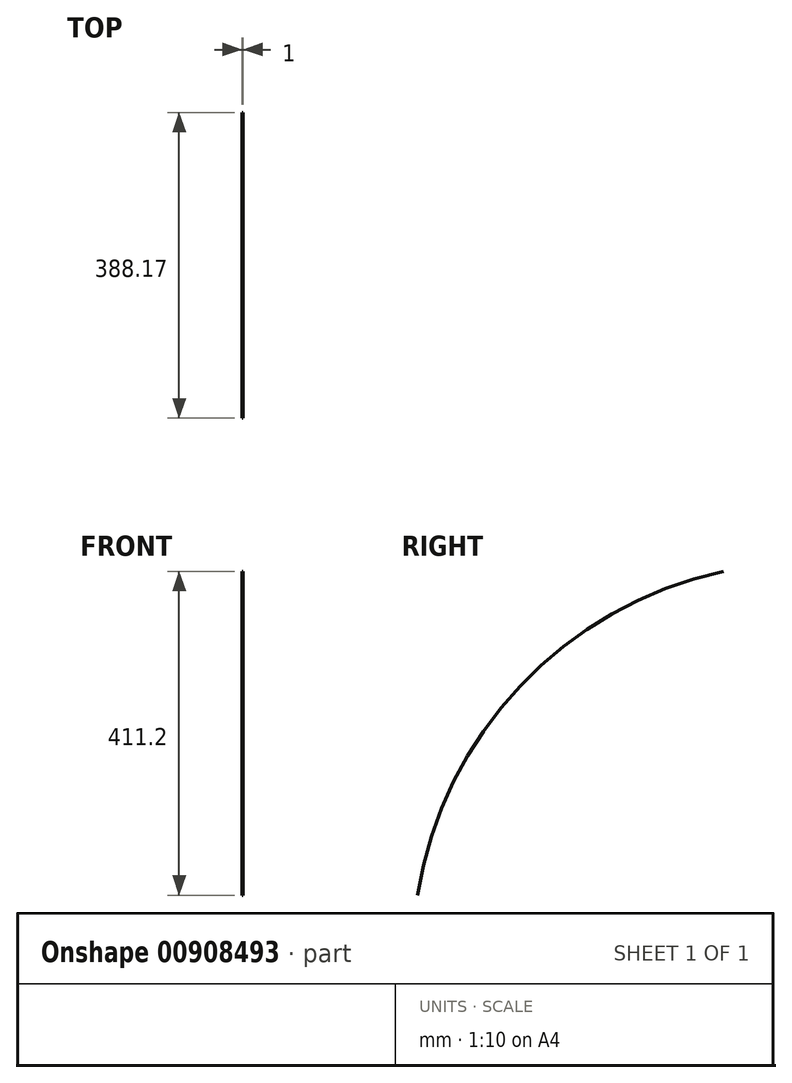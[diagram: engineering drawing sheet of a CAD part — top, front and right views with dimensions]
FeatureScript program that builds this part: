
annotation { "Feature Type Name" : "Feature", "Feature Type Description" : "" }
export const myFeature = defineFeature(function(context is Context, id is Id, definition is map)
    precondition{}
    {
        {
            var Q0;
            Q0=qCreatedBy(makeId("Right.planeOp"),FACE);
            var sketch = newSketch(context, id + "F0", { "sketchPlane" : qUnion([Q0])});
            skArc(sketch, "E0", {"start": v(-218.59, -286.4) * mm, "mid": v(-88.21, -20.65) * mm, "end": v(169.58, 124.8) * mm});
            skLineSegment(sketch, "E1", {"start": v(-218.59, -286.4) * mm, "end": v(-193.29, -189.64) * mm, "construction": true});
            skLineSegment(sketch, "E2", {"start": v(-193.29, -189.64) * mm, "end": v(-149.24, -99.87) * mm, "construction": true});
            skLineSegment(sketch, "E3", {"start": v(-149.24, -99.87) * mm, "end": v(-88.21, -20.65) * mm, "construction": true});
            skLineSegment(sketch, "E4", {"start": v(-88.21, -20.65) * mm, "end": v(-12.64, 44.84) * mm, "construction": true});
            skLineSegment(sketch, "E5", {"start": v(-12.64, 44.84) * mm, "end": v(74.45, 93.98) * mm, "construction": true});
            skLineSegment(sketch, "E6", {"start": v(74.45, 93.98) * mm, "end": v(169.58, 124.8) * mm, "construction": true});
            skLineSegment(sketch, "E7", {"start": v(-218.59, -286.4) * mm, "end": v(-317.38, -270.9) * mm, "construction": true});
            skLineSegment(sketch, "E8.1.0", {"start": v(-193.29, -189.64) * mm, "end": v(-287.02, -154.8) * mm, "construction": true});
            skLineSegment(sketch, "E8.2.0", {"start": v(-149.24, -99.87) * mm, "end": v(-234.17, -47.06) * mm, "construction": true});
            skLineSegment(sketch, "E8.3.0", {"start": v(-88.21, -20.65) * mm, "end": v(-160.93, 48) * mm, "construction": true});
            skLineSegment(sketch, "E8.4.0", {"start": v(-12.64, 44.84) * mm, "end": v(-70.24, 126.58) * mm, "construction": true});
            skLineSegment(sketch, "E8.5.0", {"start": v(74.45, 93.98) * mm, "end": v(34.27, 185.55) * mm, "construction": true});
            skLineSegment(sketch, "E8.6.0", {"start": v(169.58, 124.8) * mm, "end": v(148.42, 222.54) * mm, "construction": true});
            skSolve(sketch);
        }
        {
            var Q0;
            Q0 = qSketchRegion(id + "F0", true);
            var Q1;
            Q1=sQuery(id+"F0.wireOp",EDGE,"E0");
            extrude(context, id + "F1", {"entities" : qUnion([Q0]), "bodyType" : ToolBodyType.SURFACE, "surfaceEntities" : qUnion([Q1]), "depth" : 1 * mm, "offsetDistance" : 25 * mm});
        }
    });
